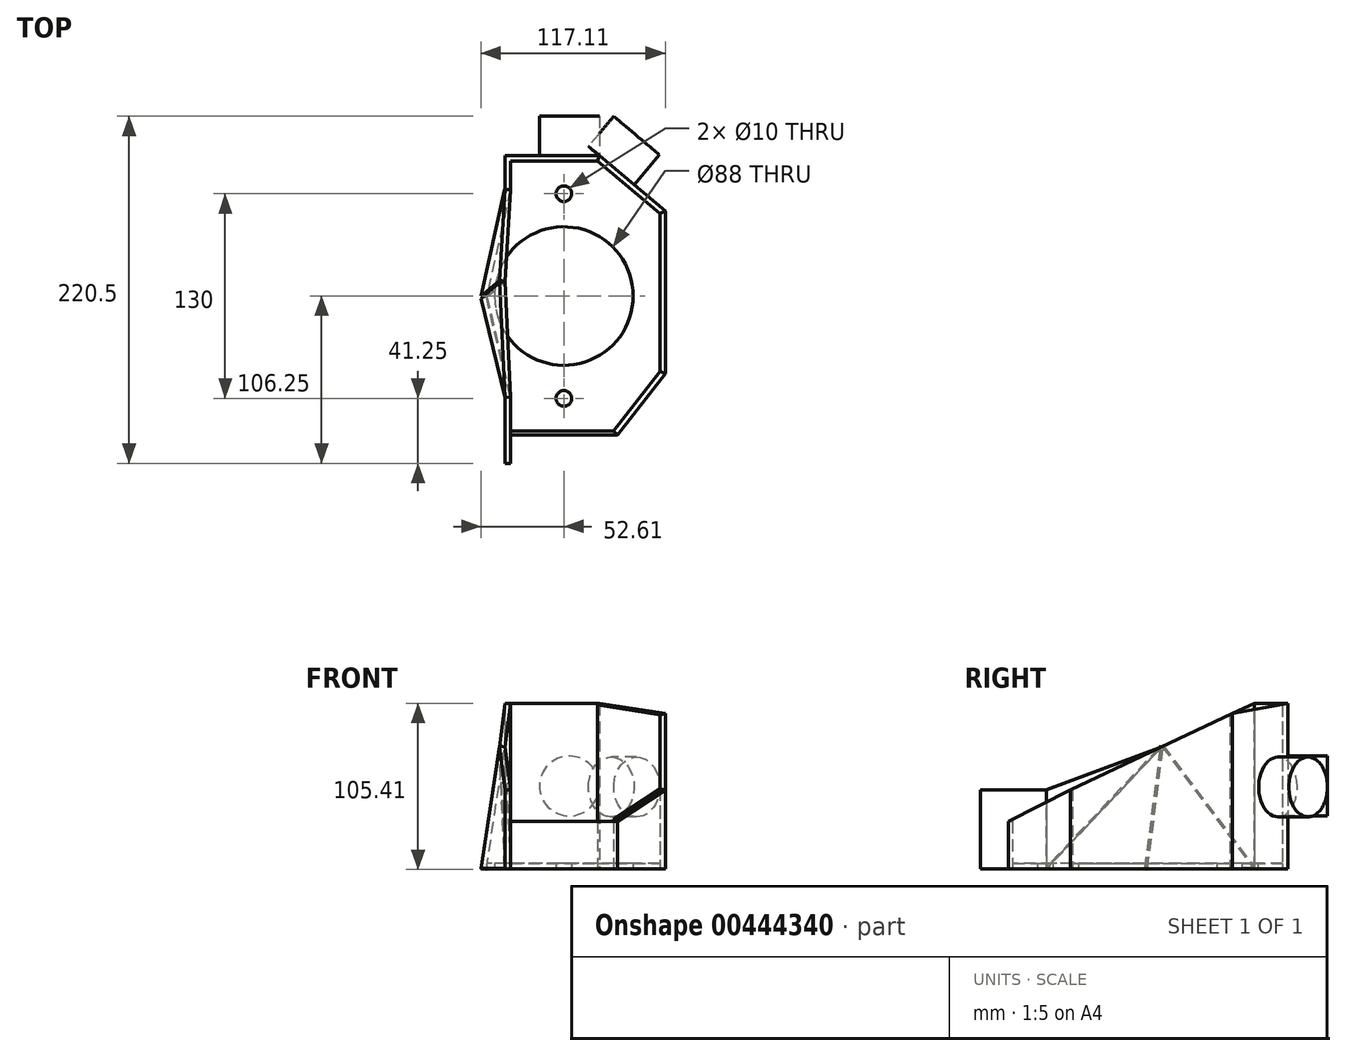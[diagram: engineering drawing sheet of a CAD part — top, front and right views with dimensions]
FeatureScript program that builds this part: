
annotation { "Feature Type Name" : "Feature", "Feature Type Description" : "" }
export const myFeature = defineFeature(function(context is Context, id is Id, definition is map)
    precondition{}
    {
        {
            var Q0;
            Q0=qCreatedBy(makeId("Top.planeOp"),FACE);
            var sketch = newSketch(context, id + "F0", { "sketchPlane" : qUnion([Q0])});
            skLineSegment(sketch, "E0", {"start": v(0, 0) * mm, "end": v(60, 0) * mm});
            skLineSegment(sketch, "E1", {"start": v(60, 0) * mm, "end": v(102, -35.36) * mm});
            skLineSegment(sketch, "E2", {"start": v(102, -138.33) * mm, "end": v(102, -35.36) * mm});
            skLineSegment(sketch, "E3", {"start": v(102, -138.33) * mm, "end": v(71.5, -177.5) * mm});
            skLineSegment(sketch, "E4", {"start": v(0, -21.5) * mm, "end": v(0, 0) * mm});
            skLineSegment(sketch, "E5", {"start": v(0, -175) * mm, "end": v(0, -195.5) * mm});
            skLineSegment(sketch, "E6", {"start": v(0, -21.5) * mm, "end": v(-15.1, -89.27) * mm});
            skLineSegment(sketch, "E7", {"start": v(-15.1, -89.27) * mm, "end": v(0, -153.5) * mm});
            skLineSegment(sketch, "E8.0", {"start": v(3.5, -21.88) * mm, "end": v(-11.5, -89.25) * mm});
            skLineSegment(sketch, "E8.1", {"start": v(3.5, -21.88) * mm, "end": v(3.5, -3.5) * mm});
            skLineSegment(sketch, "E8.2", {"start": v(-11.5, -89.25) * mm, "end": v(3.5, -153.1) * mm});
            skLineSegment(sketch, "E8.3", {"start": v(3.5, -3.5) * mm, "end": v(58.72, -3.5) * mm});
            skLineSegment(sketch, "E8.4", {"start": v(69.01, -175) * mm, "end": v(3.5, -175) * mm});
            skLineSegment(sketch, "E8.5", {"start": v(98.5, -137.13) * mm, "end": v(69.01, -175) * mm});
            skLineSegment(sketch, "E8.6", {"start": v(98.5, -137.13) * mm, "end": v(98.5, -37) * mm});
            skLineSegment(sketch, "E8.7", {"start": v(58.72, -3.5) * mm, "end": v(98.5, -37) * mm});
            skLineSegment(sketch, "E9.0", {"start": v(3.5, -177.5) * mm, "end": v(3.5, -195.5) * mm});
            skLineSegment(sketch, "E10", {"start": v(0, -21.5) * mm, "end": v(3.5, -21.5) * mm});
            skLineSegment(sketch, "E11", {"start": v(3.5, -175) * mm, "end": v(3.5, -153.1) * mm});
            skLineSegment(sketch, "E12", {"start": v(0, -153.5) * mm, "end": v(0, -175) * mm});
            skLineSegment(sketch, "E13", {"start": v(0, -153.5) * mm, "end": v(3.5, -153.5) * mm});
            skLineSegment(sketch, "E14", {"start": v(60, 0) * mm, "end": v(58.72, -3.5) * mm});
            skLineSegment(sketch, "E15", {"start": v(102, -35.36) * mm, "end": v(98.5, -37) * mm});
            skLineSegment(sketch, "E16", {"start": v(102, -138.33) * mm, "end": v(98.5, -137.13) * mm});
            skLineSegment(sketch, "E17", {"start": v(69.01, -175) * mm, "end": v(71.5, -177.5) * mm});
            skLineSegment(sketch, "E18", {"start": v(0, -195.5) * mm, "end": v(3.5, -195.5) * mm});
            skCircle(sketch, "E19", {"center": v(37.5, -89.25) * mm, "radius": 44 * mm});
            skCircle(sketch, "E20", {"center": v(37.5, -24.25) * mm, "radius": 5 * mm});
            skCircle(sketch, "E21", {"center": v(37.5, -154.25) * mm, "radius": 5 * mm});
            skLineSegment(sketch, "E22", {"start": v(37.5, -24.25) * mm, "end": v(37.5, -154.25) * mm, "construction": true});
            skLineSegment(sketch, "E23", {"start": v(3.5, -175) * mm, "end": v(0, -175) * mm});
            skLineSegment(sketch, "E24", {"start": v(71.5, -177.5) * mm, "end": v(3.5, -177.5) * mm});
            skLineSegment(sketch, "E25", {"start": v(37.5, -3.5) * mm, "end": v(37.5, -175) * mm, "construction": true});
            skLineSegment(sketch, "E26", {"start": v(3.5, -177.5) * mm, "end": v(0, -177.5) * mm});
            skSolve(sketch);
        }
        {
            var Q0;
            Q0=qCreatedBy(makeId("Right.planeOp"),FACE);
            var sketch = newSketch(context, id + "F1", { "sketchPlane" : qUnion([Q0])});
            skLineSegment(sketch, "E27", {"start": v(0, 0) * mm, "end": v(0, 105) * mm});
            skLineSegment(sketch, "E28", {"start": v(0, 105) * mm, "end": v(-21.5, 105) * mm});
            skLineSegment(sketch, "E29", {"start": v(-21.5, 105) * mm, "end": v(-138.5, 50) * mm});
            skLineSegment(sketch, "E30", {"start": v(-195.5, 30) * mm, "end": v(-195.5, 0) * mm});
            skLineSegment(sketch, "E31", {"start": v(0, 0) * mm, "end": v(-21.5, 0) * mm});
            skLineSegment(sketch, "E32", {"start": v(-195.5, 0) * mm, "end": v(-153.5, 0) * mm});
            skLineSegment(sketch, "E33", {"start": v(-21.5, 105) * mm, "end": v(-21.5, 0) * mm});
            skLineSegment(sketch, "E34", {"start": v(-153.5, 30) * mm, "end": v(-153.5, 0) * mm});
            skLineSegment(sketch, "E35", {"start": v(-153.5, 0) * mm, "end": v(-153.5, 0) * mm});
            skLineSegment(sketch, "E36.bottom", {"start": v(-195.5, 30) * mm, "end": v(-138.5, 30) * mm});
            skLineSegment(sketch, "E36.top", {"start": v(-195.5, 50) * mm, "end": v(-138.5, 50) * mm});
            skLineSegment(sketch, "E36.left", {"start": v(-195.5, 30) * mm, "end": v(-195.5, 50) * mm});
            skLineSegment(sketch, "E36.right", {"start": v(-138.5, 30) * mm, "end": v(-138.5, 50) * mm});
            skLineSegment(sketch, "E37.bottom", {"start": v(-153.5, 0) * mm, "end": v(-138.5, 0) * mm});
            skLineSegment(sketch, "E37.left", {"start": v(-153.5, 0) * mm, "end": v(-153.5, 30) * mm});
            skLineSegment(sketch, "E37.right", {"start": v(-138.5, 0) * mm, "end": v(-138.5, 30) * mm});
            skSolve(sketch);
        }
        {
            var Q0;
            Q0=sQuery(id+"F0.wireOp",VERTEX,"E7.start");
            var Q1;
            Q1=sQuery(id+"F1.wireOp",VERTEX,"E33.start");
            var Q2;
            Q2=sQuery(id+"F1.wireOp",VERTEX,"E36.top.end");
            cPlane(context, id + "F2", {"entities" : qUnion([Q0, Q1, Q2]), "cplaneType" : CPlaneType.THREE_POINT, "offset" : 25 * mm, "width" : 150 * mm, "height" : 150 * mm});
        }
        {
            var Q0;
            Q0=sQuery(id+"F1.wireOp",EDGE,"E28");
            cPlane(context, id + "F3", {"entities" : qUnion([Q0]), "cplaneType" : CPlaneType.LINE_ANGLE, "offset" : 25 * mm, "angle" : 0 * degree, "width" : 150 * mm, "height" : 150 * mm});
        }
        {
            var Q0;
            Q0=sQuery(id+"F1.wireOp",EDGE,"E29");
            cPlane(context, id + "F4", {"entities" : qUnion([Q0]), "cplaneType" : CPlaneType.LINE_ANGLE, "offset" : 25 * mm, "angle" : 0 * degree, "width" : 150 * mm, "height" : 150 * mm});
        }
        {
            var Q0;
            Q0=sQuery(id+"F1.wireOp",EDGE,"E36.bottom");
            cPlane(context, id + "F5", {"entities" : qUnion([Q0]), "cplaneType" : CPlaneType.LINE_ANGLE, "offset" : 25 * mm, "angle" : 0 * degree, "width" : 150 * mm, "height" : 150 * mm});
        }
        {
            var Q0;
            Q0=makeQuery(id+"F0.imprint","IMPRINT",FACE,{"disambiguationData":[TD([[makeQuery(id+"F0.imprint","IMPRINT",EDGE,{"derivedFrom":sQuery(id+"F0.wireOp",EDGE,"E8.4")}),1.0]])]});
            var Q1;
            Q1=makeQuery(id+"F0.imprint","IMPRINT",FACE,{"disambiguationData":[TD([[makeQuery(id+"F0.imprint","IMPRINT",EDGE,{"derivedFrom":sQuery(id+"F0.wireOp",EDGE,"E9.0")}),-1.0]])]});
            var Q2;
            Q2=qCreatedBy(id+"F5.planeOp",FACE);
            extrude(context, id + "F6", {"entities" : qUnion([Q0, Q1]), "endBound" : BoundingType.UP_TO_SURFACE, "endBoundEntityFace" : qUnion([Q2]), "depth" : 25 * mm});
        }
        {
            var Q0;
            Q0=makeQuery(id+"F0.imprint","IMPRINT",FACE,{"disambiguationData":[TD([[makeQuery(id+"F0.imprint","IMPRINT",EDGE,{"derivedFrom":sQuery(id+"F0.wireOp",EDGE,"E2")}),1.0]])]});
            var Q1;
            Q1=qCreatedBy(id+"F4.planeOp",FACE);
            extrude(context, id + "F7", {"entities" : qUnion([Q0]), "endBound" : BoundingType.UP_TO_SURFACE, "endBoundEntityFace" : qUnion([Q1]), "depth" : 25 * mm});
        }
        {
            var Q0;
            Q0=makeQuery(id+"F0.imprint","IMPRINT",FACE,{"disambiguationData":[TD([[makeQuery(id+"F0.imprint","IMPRINT",EDGE,{"derivedFrom":sQuery(id+"F0.wireOp",EDGE,"E0")}),-1.0]])]});
            var Q1;
            Q1=qCreatedBy(id+"F3.planeOp",FACE);
            extrude(context, id + "F8", {"entities" : qUnion([Q0]), "endBound" : BoundingType.UP_TO_SURFACE, "endBoundEntityFace" : qUnion([Q1]), "depth" : 25 * mm});
        }
        {
            var Q0;
            Q0=makeQuery(id+"F8.opExtrude","CAP_VERTEX",VERTEX,{"disambiguationData":[OSD([sQuery(id+"F0.wireOp",EDGE,"E0"),sQuery(id+"F0.wireOp",EDGE,"E14")])],"isStart":false});
            var Q1;
            Q1=makeQuery(id+"F7.opExtrude","CAP_VERTEX",VERTEX,{"disambiguationData":[OSD([sQuery(id+"F0.wireOp",EDGE,"E2"),sQuery(id+"F0.wireOp",EDGE,"E15")])],"isStart":false});
            var Q2;
            Q2=makeQuery(id+"F7.opExtrude","CAP_VERTEX",VERTEX,{"disambiguationData":[OSD([sQuery(id+"F0.wireOp",EDGE,"E8.6"),sQuery(id+"F0.wireOp",EDGE,"E15")])],"isStart":false});
            cPlane(context, id + "F9", {"entities" : qUnion([Q0, Q1, Q2]), "cplaneType" : CPlaneType.THREE_POINT, "offset" : 25 * mm, "width" : 150 * mm, "height" : 150 * mm});
        }
        {
            var Q0;
            Q0=makeQuery(id+"F0.imprint","IMPRINT",FACE,{"disambiguationData":[TD([[makeQuery(id+"F0.imprint","IMPRINT",EDGE,{"derivedFrom":sQuery(id+"F0.wireOp",EDGE,"E1")}),-1.0]])]});
            var Q1;
            Q1=qCreatedBy(id+"F9.planeOp",FACE);
            extrude(context, id + "F10", {"entities" : qUnion([Q0]), "operationType" : NewBodyOperationType.ADD, "endBound" : BoundingType.UP_TO_SURFACE, "endBoundEntityFace" : qUnion([Q1]), "depth" : 25 * mm});
        }
        {
            var Q0;
            Q0=makeQuery(id+"F7.opExtrude","CAP_VERTEX",VERTEX,{"disambiguationData":[OSD([sQuery(id+"F0.wireOp",EDGE,"E8.6"),sQuery(id+"F0.wireOp",EDGE,"E16")])],"isStart":false});
            var Q1;
            Q1=makeQuery(id+"F7.opExtrude","CAP_VERTEX",VERTEX,{"disambiguationData":[OSD([sQuery(id+"F0.wireOp",EDGE,"E2"),sQuery(id+"F0.wireOp",EDGE,"E16")])],"isStart":false});
            var Q2;
            Q2=makeQuery(id+"F6.opExtrude","CAP_VERTEX",VERTEX,{"disambiguationData":[OSD([sQuery(id+"F0.wireOp",EDGE,"E17"),sQuery(id+"F0.wireOp",EDGE,"E24")])],"isStart":false});
            cPlane(context, id + "F11", {"entities" : qUnion([Q0, Q1, Q2]), "cplaneType" : CPlaneType.THREE_POINT, "offset" : 25 * mm, "width" : 150 * mm, "height" : 150 * mm});
        }
        {
            var Q0;
            Q0=makeQuery(id+"F0.imprint","IMPRINT",FACE,{"disambiguationData":[TD([[makeQuery(id+"F0.imprint","IMPRINT",EDGE,{"derivedFrom":sQuery(id+"F0.wireOp",EDGE,"E3")}),-1.0]])]});
            var Q1;
            Q1=qCreatedBy(id+"F11.planeOp",FACE);
            extrude(context, id + "F12", {"entities" : qUnion([Q0]), "operationType" : NewBodyOperationType.ADD, "endBound" : BoundingType.UP_TO_SURFACE, "endBoundEntityFace" : qUnion([Q1]), "depth" : 25 * mm});
        }
        {
            var Q0;
            Q0=makeQuery(id+"F8.opExtrude","SWEPT_FACE",FACE,{"disambiguationData":[OSD([sQuery(id+"F0.wireOp",EDGE,"E0")])]});
            var sketch = newSketch(context, id + "F13", { "sketchPlane" : qUnion([Q0])});
            skCircle(sketch, "E38", {"center": v(-41, 52.5) * mm, "radius": 19 * mm});
            skLineSegment(sketch, "E39", {"start": v(-41, 105) * mm, "end": v(-41, 0) * mm, "construction": true});
            skSolve(sketch);
        }
        {
            var Q0;
            Q0=makeQuery(id+"F10.opExtrude","SWEPT_FACE",FACE,{"disambiguationData":[OSD([sQuery(id+"F0.wireOp",EDGE,"E1")])]});
            var sketch = newSketch(context, id + "F14", { "sketchPlane" : qUnion([Q0])});
            skCircle(sketch, "E40", {"center": v(-55.9, 51.9) * mm, "radius": 19 * mm});
            skLineSegment(sketch, "E41", {"start": v(-55.9, 0) * mm, "end": v(-55.9, 103.81) * mm, "construction": true});
            skSolve(sketch);
        }
        {
            var Q0;
            Q0=makeQuery(id+"F13.imprint","IMPRINT",FACE,{"disambiguationData":[TD([[makeQuery(id+"F13.imprint","IMPRINT",EDGE,{"derivedFrom":sQuery(id+"F13.wireOp",EDGE,"E38")}),1.0]])]});
            extrude(context, id + "F15", {"entities" : qUnion([Q0]), "depth" : 25 * mm});
        }
        {
            var Q0;
            {var subQ0=sQuery(id+"F14.wireOp",EDGE,"E40");var subQ1=sQuery(id+"F0.wireOp",EDGE,"E14");var subQ2=sQuery(id+"F0.wireOp",EDGE,"E1");var subQ3=sQuery(id+"F0.wireOp",EDGE,"E0");var subQ4=makeQuery(id+"F10.boolean.opBoolean","MERGE",EDGE,{"derivedFrom":[makeQuery(id+"F8.opExtrude","SWEPT_EDGE",EDGE,{"disambiguationData":[OSD([subQ3,subQ2,subQ1])]}),makeQuery(id+"F10.opExtrude","SWEPT_EDGE",EDGE,{"disambiguationData":[OSD([subQ3,subQ2,subQ1])]})]});var subQ5=makeQuery(id+"F14.imprint","INTERSECT",VERTEX,{"disambiguationData":[OD(0.0)],"derivedFrom":[subQ4,subQ0]});Q0=makeQuery(id+"F14.imprint","IMPRINT",FACE,{"disambiguationData":[TD([[makeQuery(id+"F14.imprint","IMPRINT",EDGE,{"disambiguationData":[TD([[subQ5,1.0]])],"derivedFrom":subQ0}),1.0]])]});}
            var Q1;
            {var subQ0=sQuery(id+"F14.wireOp",EDGE,"E40");var subQ1=sQuery(id+"F0.wireOp",EDGE,"E14");var subQ2=sQuery(id+"F0.wireOp",EDGE,"E1");var subQ3=sQuery(id+"F0.wireOp",EDGE,"E0");var subQ4=makeQuery(id+"F10.boolean.opBoolean","MERGE",EDGE,{"derivedFrom":[makeQuery(id+"F8.opExtrude","SWEPT_EDGE",EDGE,{"disambiguationData":[OSD([subQ3,subQ2,subQ1])]}),makeQuery(id+"F10.opExtrude","SWEPT_EDGE",EDGE,{"disambiguationData":[OSD([subQ3,subQ2,subQ1])]})]});var subQ5=makeQuery(id+"F14.imprint","INTERSECT",VERTEX,{"disambiguationData":[OD(0.0)],"derivedFrom":[subQ4,subQ0]});Q1=makeQuery(id+"F14.imprint","IMPRINT",FACE,{"disambiguationData":[TD([[makeQuery(id+"F14.imprint","IMPRINT",EDGE,{"disambiguationData":[TD([[subQ5,-1.0]])],"derivedFrom":subQ0}),1.0]])]});}
            extrude(context, id + "F16", {"entities" : qUnion([Q0, Q1]), "depth" : 25 * mm});
        }
        {
            var Q0;
            {var subQ4=sQuery(id+"F0.wireOp",EDGE,"E8.0");Q0=makeQuery(id+"F0.imprint","IMPRINT",FACE,{"disambiguationData":[TD([[makeQuery(id+"F0.imprint","IMPRINT",EDGE,{"derivedFrom":subQ4}),1.0]])]});}
            extrude(context, id + "F17", {"entities" : qUnion([Q0]), "depth" : 3.5 * mm});
        }
        {
            var Q0;
            Q0=sQuery(id+"F1.wireOp",EDGE,"E29");
            cPoint(context, id + "F18", {"entities" : qUnion([Q0]), "parameter" : 0.5});
        }
        {
            var Q0;
            Q0 = qCreatedBy(id + "F18" ,VERTEX);
            var Q1;
            Q1=makeQuery(id+"F17.opExtrude","CAP_VERTEX",VERTEX,{"disambiguationData":[OSD([sQuery(id+"F0.wireOp",EDGE,"E8.0"),sQuery(id+"F0.wireOp",EDGE,"E8.2")])],"isStart":true});
            var Q2;
            Q2=makeQuery(id+"F17.opExtrude","CAP_VERTEX",VERTEX,{"disambiguationData":[OSD([sQuery(id+"F0.wireOp",EDGE,"E8.0"),sQuery(id+"F0.wireOp",EDGE,"E8.1")])],"isStart":true});
            cPlane(context, id + "F19", {"entities" : qUnion([Q0, Q1, Q2]), "cplaneType" : CPlaneType.THREE_POINT, "offset" : 25 * mm, "width" : 150 * mm, "height" : 150 * mm});
        }
        {
            var Q0;
            Q0=qCreatedBy(id+"F19.planeOp",FACE);
            var sketch = newSketch(context, id + "F20", { "sketchPlane" : qUnion([Q0])});
            skLineSegment(sketch, "E42", {"start": v(20.62, 0.42) * mm, "end": v(90.4, -1.82) * mm});
            skLineSegment(sketch, "E43", {"start": v(90.4, -1.82) * mm, "end": v(80.14, 76.93) * mm});
            skLineSegment(sketch, "E44", {"start": v(80.14, 76.93) * mm, "end": v(20.62, 0.42) * mm});
            skSolve(sketch);
        }
        {
            var Q0;
            Q0=makeQuery(id+"F20.imprint","IMPRINT",FACE,{"disambiguationData":[TD([[makeQuery(id+"F20.imprint","IMPRINT",EDGE,{"derivedFrom":sQuery(id+"F20.wireOp",EDGE,"E42")}),1.0]])]});
            extrude(context, id + "F21", {"entities" : qUnion([Q0]), "depth" : 3.5 * mm});
        }
        {
            var Q0;
            Q0=makeQuery(id+"F0.imprint","IMPRINT",FACE,{"disambiguationData":[TD([[makeQuery(id+"F0.imprint","IMPRINT",EDGE,{"derivedFrom":sQuery(id+"F0.wireOp",EDGE,"E12")}),1.0]])]});
            var Q1;
            Q1=qCreatedBy(id+"F5.planeOp",FACE);
            extrude(context, id + "F22", {"entities" : qUnion([Q0]), "endBoundEntityFace" : qUnion([Q1]), "depth" : 50 * mm});
        }
        {
            var Q0;
            Q0=sQuery(id+"F1.wireOp",EDGE,"E29");
            cPoint(context, id + "F23", {"entities" : qUnion([Q0]), "parameter" : 0.5});
        }
        {
            var Q0;
            Q0=makeQuery(id+"F21.opExtrude","CAP_VERTEX",VERTEX,{"disambiguationData":[OSD([sQuery(id+"F20.wireOp",EDGE,"E42"),sQuery(id+"F20.wireOp",EDGE,"E43")])],"isStart":true});
            var Q1;
            Q1=makeQuery(id+"F22.opExtrude","CAP_VERTEX",VERTEX,{"disambiguationData":[OSD([sQuery(id+"F0.wireOp",EDGE,"E11"),sQuery(id+"F0.wireOp",EDGE,"E13")])],"isStart":true});
            var Q2;
            Q2 = qCreatedBy(id + "F23" ,VERTEX);
            cPlane(context, id + "F24", {"entities" : qUnion([Q0, Q1, Q2]), "cplaneType" : CPlaneType.THREE_POINT, "offset" : 25 * mm, "width" : 150 * mm, "height" : 150 * mm});
        }
        {
            var Q0;
            Q0=qCreatedBy(id+"F24.planeOp",FACE);
            var sketch = newSketch(context, id + "F25", { "sketchPlane" : qUnion([Q0])});
            skLineSegment(sketch, "E45", {"start": v(-85.02, -2.5) * mm, "end": v(-74.72, 76.26) * mm});
            skLineSegment(sketch, "E46", {"start": v(-74.72, 76.26) * mm, "end": v(-149.83, 0.62) * mm});
            skLineSegment(sketch, "E47", {"start": v(-149.83, 0.62) * mm, "end": v(-85.02, -2.5) * mm});
            skSolve(sketch);
        }
        {
            var Q0;
            Q0=makeQuery(id+"F25.imprint","IMPRINT",FACE,{"disambiguationData":[TD([[makeQuery(id+"F25.imprint","IMPRINT",EDGE,{"derivedFrom":sQuery(id+"F25.wireOp",EDGE,"E45")}),1.0]])]});
            extrude(context, id + "F26", {"entities" : qUnion([Q0]), "oppositeDirection" : true, "depth" : 3.5 * mm});
        }
        {
            var Q0;
            Q0=sQuery(id+"F1.wireOp",EDGE,"E29");
            cPoint(context, id + "F27", {"entities" : qUnion([Q0]), "parameter" : 0.5});
        }
        {
            var Q0;
            Q0=makeQuery(id+"F8.opExtrude","CAP_VERTEX",VERTEX,{"disambiguationData":[OSD([sQuery(id+"F0.wireOp",EDGE,"E8.1"),sQuery(id+"F0.wireOp",EDGE,"E10")])],"isStart":false});
            var Q1;
            Q1 = qCreatedBy(id + "F27" ,VERTEX);
            var Q2;
            Q2=makeQuery(id+"F8.opExtrude","CAP_VERTEX",VERTEX,{"disambiguationData":[OSD([sQuery(id+"F0.wireOp",EDGE,"E8.1"),sQuery(id+"F0.wireOp",EDGE,"E10")])],"isStart":true});
            cPlane(context, id + "F28", {"entities" : qUnion([Q0, Q1, Q2]), "cplaneType" : CPlaneType.THREE_POINT, "offset" : 25 * mm, "width" : 150 * mm, "height" : 150 * mm});
        }
        {
            var Q0;
            Q0=qCreatedBy(id+"F28.planeOp",FACE);
            var sketch = newSketch(context, id + "F29", { "sketchPlane" : qUnion([Q0])});
            skLineSegment(sketch, "E48", {"start": v(21.25, 105) * mm, "end": v(79.86, 77.5) * mm});
            skLineSegment(sketch, "E49", {"start": v(79.86, 77.5) * mm, "end": v(21.25, 0) * mm});
            skLineSegment(sketch, "E50", {"start": v(21.25, 0) * mm, "end": v(21.25, 105) * mm});
            skSolve(sketch);
        }
        {
            var Q0;
            Q0=makeQuery(id+"F29.imprint","IMPRINT",FACE,{"disambiguationData":[TD([[makeQuery(id+"F29.imprint","IMPRINT",EDGE,{"derivedFrom":sQuery(id+"F29.wireOp",EDGE,"E48")}),-1.0]])]});
            extrude(context, id + "F30", {"entities" : qUnion([Q0]), "depth" : 3.5 * mm});
        }
        {
            var Q0;
            Q0=sQuery(id+"F1.wireOp",EDGE,"E29");
            cPoint(context, id + "F31", {"entities" : qUnion([Q0]), "parameter" : 0.5});
        }
        {
            var Q0;
            Q0 = qCreatedBy(id + "F31" ,VERTEX);
            var Q1;
            Q1=makeQuery(id+"F22.opExtrude","CAP_VERTEX",VERTEX,{"disambiguationData":[OSD([sQuery(id+"F0.wireOp",EDGE,"E11"),sQuery(id+"F0.wireOp",EDGE,"E13")])],"isStart":false});
            var Q2;
            Q2=makeQuery(id+"F22.opExtrude","CAP_VERTEX",VERTEX,{"disambiguationData":[OSD([sQuery(id+"F0.wireOp",EDGE,"E11"),sQuery(id+"F0.wireOp",EDGE,"E13")])],"isStart":true});
            cPlane(context, id + "F32", {"entities" : qUnion([Q0, Q1, Q2]), "cplaneType" : CPlaneType.THREE_POINT, "offset" : 25 * mm, "width" : 150 * mm, "height" : 150 * mm});
        }
        {
            var Q0;
            Q0=qCreatedBy(id+"F32.planeOp",FACE);
            var sketch = newSketch(context, id + "F33", { "sketchPlane" : qUnion([Q0])});
            skLineSegment(sketch, "E51", {"start": v(79.9, 77.5) * mm, "end": v(153.5, 50) * mm});
            skLineSegment(sketch, "E52", {"start": v(153.5, 50) * mm, "end": v(153.5, 0) * mm});
            skLineSegment(sketch, "E53", {"start": v(153.5, 0) * mm, "end": v(79.9, 77.5) * mm});
            skSolve(sketch);
        }
        {
            var Q0;
            Q0=makeQuery(id+"F33.imprint","IMPRINT",FACE,{"disambiguationData":[TD([[makeQuery(id+"F33.imprint","IMPRINT",EDGE,{"derivedFrom":sQuery(id+"F33.wireOp",EDGE,"E51")}),-1.0]])]});
            extrude(context, id + "F34", {"entities" : qUnion([Q0]), "depth" : 3.5 * mm});
        }
        {
            var Q0;
            Q0=makeQuery(id+"F22.opExtrude","SWEPT_FACE",FACE,{"disambiguationData":[OSD([sQuery(id+"F0.wireOp",EDGE,"E23")])]});
            var sketch = newSketch(context, id + "F35", { "sketchPlane" : qUnion([Q0])});
            skLineSegment(sketch, "E54.bottom", {"start": v(0, 50) * mm, "end": v(3.5, 50) * mm});
            skLineSegment(sketch, "E54.top", {"start": v(0, 30) * mm, "end": v(3.5, 30) * mm});
            skLineSegment(sketch, "E54.left", {"start": v(0, 50) * mm, "end": v(0, 30) * mm});
            skLineSegment(sketch, "E54.right", {"start": v(3.5, 50) * mm, "end": v(3.5, 30) * mm});
            skSolve(sketch);
        }
        {
            var Q0;
            Q0=makeQuery(id+"F35.imprint","IMPRINT",FACE,{"disambiguationData":[TD([[makeQuery(id+"F35.imprint","IMPRINT",EDGE,{"derivedFrom":sQuery(id+"F35.wireOp",EDGE,"E54.bottom")}),1.0]])]});
            var Q1;
            Q1=makeQuery(id+"F6.opExtrude","SWEPT_FACE",FACE,{"disambiguationData":[OSD([sQuery(id+"F0.wireOp",EDGE,"E18")])]});
            extrude(context, id + "F36", {"entities" : qUnion([Q0]), "operationType" : NewBodyOperationType.ADD, "endBound" : BoundingType.UP_TO_SURFACE, "endBoundEntityFace" : qUnion([Q1]), "depth" : 25 * mm});
        }
    });
